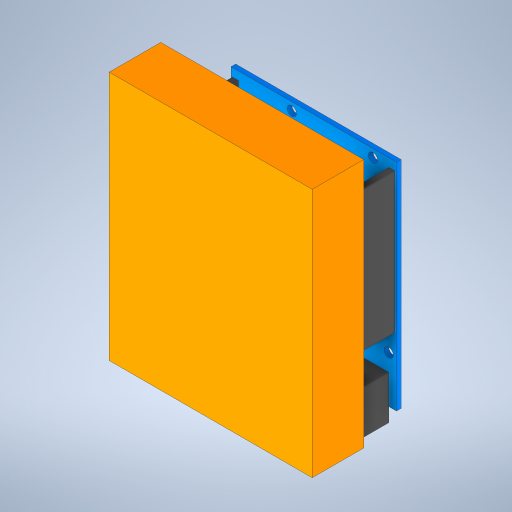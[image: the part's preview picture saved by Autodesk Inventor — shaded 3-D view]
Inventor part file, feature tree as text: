
AUTODESK INVENTOR PART (.ipt)
format: ipt  version: 2023 (Build 270158000, 158)  size: 287,744 bytes
history: native  units: mm
features: extrude x5, sketch x3, other x1
ambient origin geometry x8: Origin, YZ Plane, XZ Plane, XY Plane, X Axis, Y Axis, Z Axis, Center Point
bodies: Body1 (feature_tree)
feature tree (9):
  other  "솔리드1"
  extrude  "돌출1"  Depth=53.0mm
  sketch  "스케치3"
  extrude  "돌출2"  Depth=69.0mm
  extrude  "돌출3"  Depth=3.0mm
  extrude  "돌출4"  Depth=3.0mm
  extrude  "돌출5"  Depth=2.5mm
  sketch  "스케치2"
  sketch  "스케치4"
